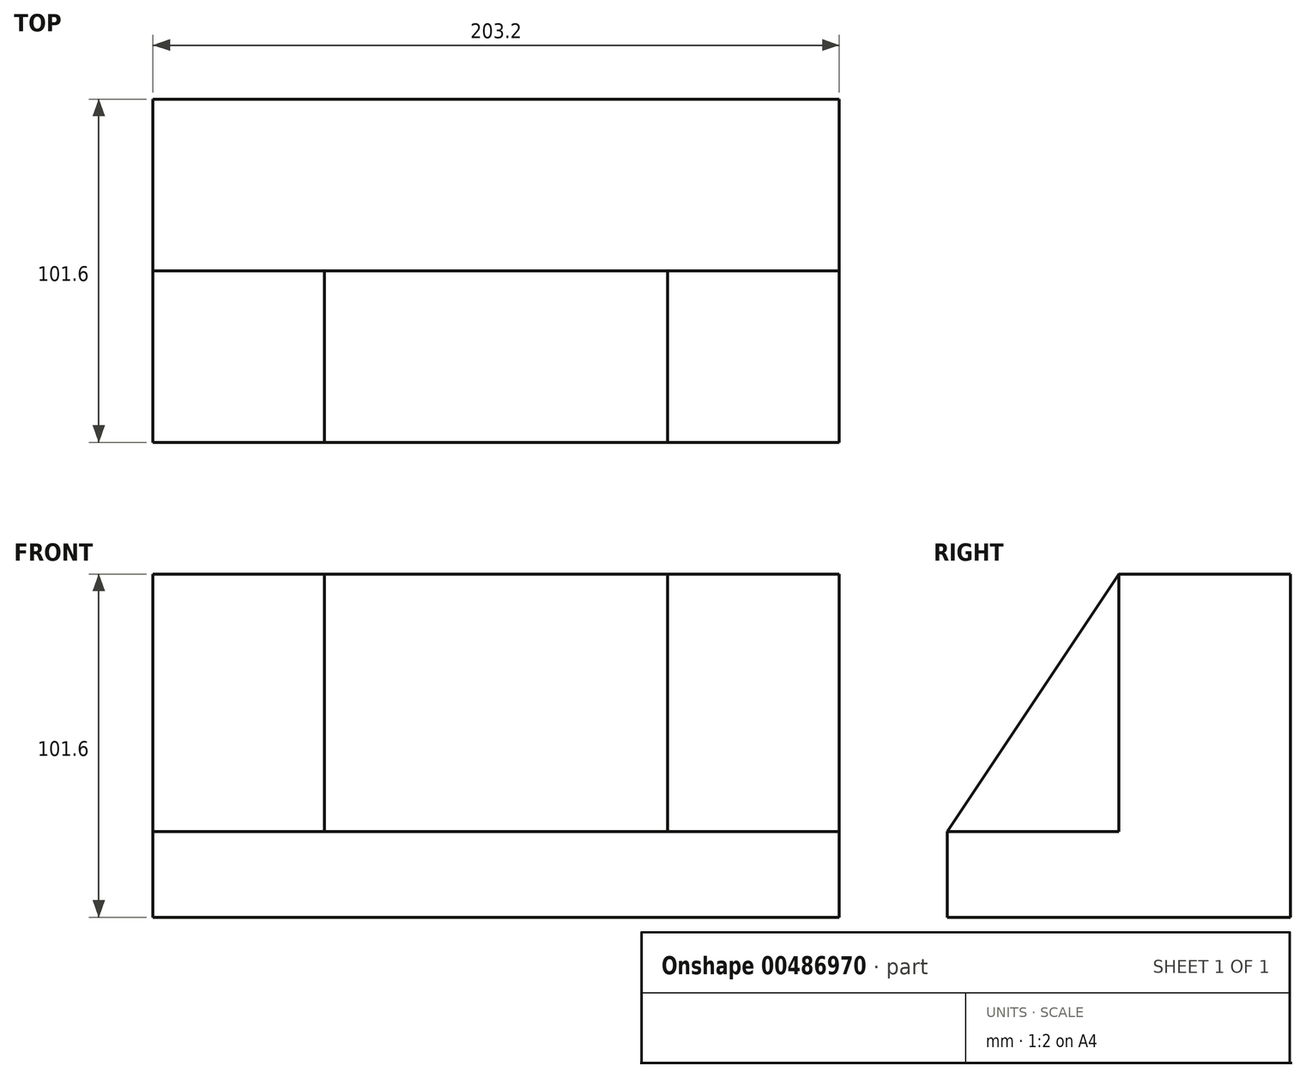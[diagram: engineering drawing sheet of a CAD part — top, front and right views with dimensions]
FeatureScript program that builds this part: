
annotation { "Feature Type Name" : "Feature", "Feature Type Description" : "" }
export const myFeature = defineFeature(function(context is Context, id is Id, definition is map)
    precondition{}
    {
        {
            var Q0;
            Q0=qCreatedBy(makeId("Front.planeOp"),FACE);
            var sketch = newSketch(context, id + "F0", { "sketchPlane" : qUnion([Q0])});
            skLineSegment(sketch, "E0.bottom", {"start": v(0, 0) * mm, "end": v(-203.2, 0) * mm});
            skLineSegment(sketch, "E0.top", {"start": v(0, 101.6) * mm, "end": v(-203.2, 101.6) * mm});
            skLineSegment(sketch, "E0.left", {"start": v(0, 0) * mm, "end": v(0, 101.6) * mm});
            skLineSegment(sketch, "E0.right", {"start": v(-203.2, 0) * mm, "end": v(-203.2, 101.6) * mm});
            skSolve(sketch);
        }
        {
            var Q0;
            Q0=makeQuery(id+"F0.imprint","IMPRINT",FACE,{"disambiguationData":[TD([[makeQuery(id+"F0.imprint","IMPRINT",EDGE,{"derivedFrom":sQuery(id+"F0.wireOp",EDGE,"E0.bottom")}),-1.0]])]});
            var Q1;
            Q1 = qSketchRegion(id + "F2", true);
            extrude(context, id + "F1", {"entities" : qUnion([Q0, Q1]), "depth" : 50.8 * mm});
        }
        {
            var Q0;
            Q0=makeQuery(id+"F1.opExtrude","CAP_FACE",FACE,{"disambiguationData":[OSD([sQuery(id+"F0.wireOp",EDGE,"E0.bottom"),sQuery(id+"F0.wireOp",EDGE,"E0.top"),sQuery(id+"F0.wireOp",EDGE,"E0.left"),sQuery(id+"F0.wireOp",EDGE,"E0.right")])],"isStart":false});
            var sketch = newSketch(context, id + "F2", { "sketchPlane" : qUnion([Q0])});
            skLineSegment(sketch, "E1.bottom", {"start": v(-203.2, 0) * mm, "end": v(0, 0) * mm});
            skLineSegment(sketch, "E1.top", {"start": v(-203.2, 25.4) * mm, "end": v(0, 25.4) * mm});
            skLineSegment(sketch, "E1.left", {"start": v(-203.2, 0) * mm, "end": v(-203.2, 25.4) * mm});
            skLineSegment(sketch, "E1.right", {"start": v(0, 0) * mm, "end": v(0, 25.4) * mm});
            skSolve(sketch);
        }
        {
            var Q0;
            Q0=makeQuery(id+"F2.imprint","IMPRINT",FACE,{"disambiguationData":[TD([[makeQuery(id+"F2.imprint","IMPRINT",EDGE,{"derivedFrom":sQuery(id+"F2.wireOp",EDGE,"E1.bottom")}),-1.0]])]});
            extrude(context, id + "F3", {"entities" : qUnion([Q0]), "operationType" : NewBodyOperationType.ADD, "depth" : 50.8 * mm});
        }
        {
            var Q0;
            Q0=makeQuery(id+"F3.boolean.opBoolean","MERGE",FACE,{"derivedFrom":[makeQuery(id+"F1.opExtrude","SWEPT_FACE",FACE,{"disambiguationData":[OSD([sQuery(id+"F0.wireOp",EDGE,"E0.right")])]}),makeQuery(id+"F3.opExtrude","SWEPT_FACE",FACE,{"disambiguationData":[OSD([sQuery(id+"F2.wireOp",EDGE,"E1.left")])]})]});
            var sketch = newSketch(context, id + "F4", { "sketchPlane" : qUnion([Q0])});
            skLineSegment(sketch, "E2", {"start": v(50.8, 101.6) * mm, "end": v(101.6, 25.4) * mm});
            skLineSegment(sketch, "E3", {"start": v(101.6, 25.4) * mm, "end": v(50.8, 25.4) * mm});
            skSolve(sketch);
        }
        {
            var Q0;
            Q0=makeQuery(id+"F4.imprint","IMPRINT",FACE,{"disambiguationData":[TD([[makeQuery(id+"F4.imprint","IMPRINT",EDGE,{"derivedFrom":sQuery(id+"F4.wireOp",EDGE,"E2")}),-1.0]])]});
            extrude(context, id + "F5", {"entities" : qUnion([Q0]), "oppositeDirection" : true, "depth" : 50.8 * mm});
        }
        {
            var Q0;
            Q0=makeQuery(id+"F3.boolean.opBoolean","MERGE",FACE,{"derivedFrom":[makeQuery(id+"F1.opExtrude","SWEPT_FACE",FACE,{"disambiguationData":[OSD([sQuery(id+"F0.wireOp",EDGE,"E0.left")])]}),makeQuery(id+"F3.opExtrude","SWEPT_FACE",FACE,{"disambiguationData":[OSD([sQuery(id+"F2.wireOp",EDGE,"E1.right")])]})]});
            var sketch = newSketch(context, id + "F6", { "sketchPlane" : qUnion([Q0])});
            skLineSegment(sketch, "E4", {"start": v(-50.8, 101.6) * mm, "end": v(-101.6, 25.4) * mm});
            skLineSegment(sketch, "E5", {"start": v(-101.6, 25.4) * mm, "end": v(-50.8, 25.4) * mm});
            skLineSegment(sketch, "E6", {"start": v(-50.8, 25.4) * mm, "end": v(-50.8, 101.6) * mm});
            skSolve(sketch);
        }
        {
            var Q0;
            Q0=makeQuery(id+"F6.imprint","IMPRINT",FACE,{"disambiguationData":[TD([[makeQuery(id+"F6.imprint","IMPRINT",EDGE,{"derivedFrom":sQuery(id+"F6.wireOp",EDGE,"E4")}),1.0]])]});
            extrude(context, id + "F7", {"entities" : qUnion([Q0]), "oppositeDirection" : true, "depth" : 50.8 * mm});
        }
    });
